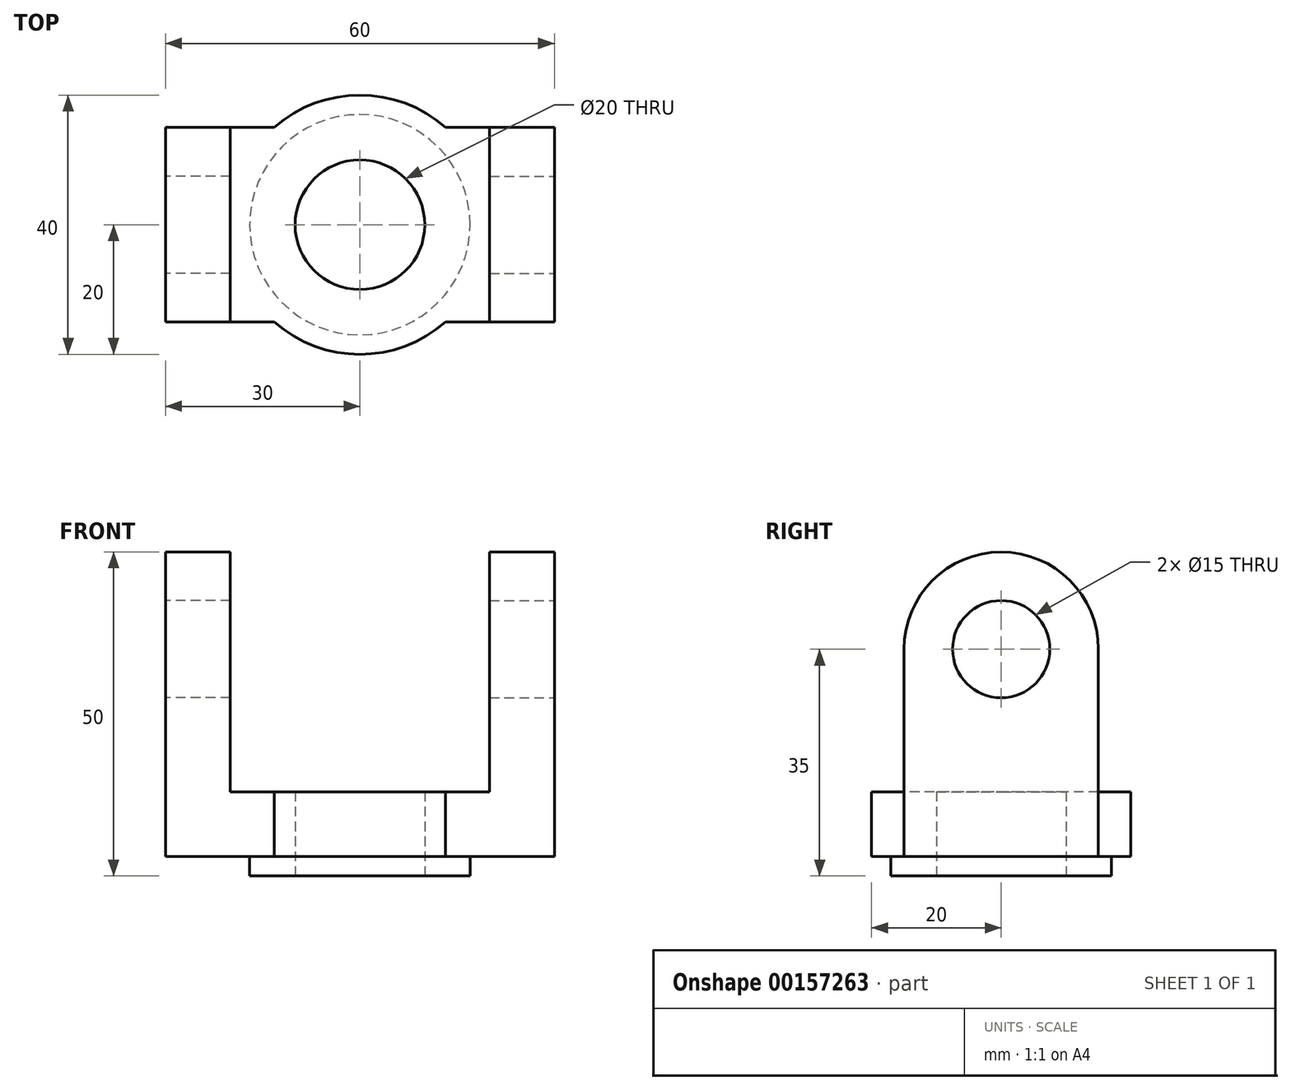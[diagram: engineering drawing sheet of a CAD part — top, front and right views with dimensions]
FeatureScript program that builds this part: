
annotation { "Feature Type Name" : "Feature", "Feature Type Description" : "" }
export const myFeature = defineFeature(function(context is Context, id is Id, definition is map)
    precondition{}
    {
        {
            var Q0;
            Q0=qCreatedBy(makeId("Top.planeOp"),FACE);
            var sketch = newSketch(context, id + "F0", { "sketchPlane" : qUnion([Q0])});
            skCircle(sketch, "E0", {"center": v(0, 0) * mm, "radius": 10 * mm});
            skArc(sketch, "E1", {"start": v(-13.23, -15) * mm, "mid": v(0, -20) * mm, "end": v(13.23, -15) * mm});
            skLineSegment(sketch, "E2.bottom", {"start": v(30, 15) * mm, "end": v(13.23, 15) * mm});
            skLineSegment(sketch, "E2.top", {"start": v(30, -15) * mm, "end": v(13.23, -15) * mm});
            skLineSegment(sketch, "E2.left", {"start": v(30, 15) * mm, "end": v(30, -15) * mm});
            skLineSegment(sketch, "E2.right", {"start": v(-30, 15) * mm, "end": v(-30, -15) * mm});
            skArc(sketch, "E3.trimOffspring", {"start": v(13.23, 15) * mm, "mid": v(0, 20) * mm, "end": v(-13.23, 15) * mm});
            skLineSegment(sketch, "E4.trimOffspring", {"start": v(-13.23, -15) * mm, "end": v(-30, -15) * mm});
            skLineSegment(sketch, "E5.trimOffspring", {"start": v(-13.23, 15) * mm, "end": v(-30, 15) * mm});
            skSolve(sketch);
        }
        {
            var Q0;
            Q0 = qSketchRegion(id + "F0", true);
            extrude(context, id + "F1", {"entities" : qUnion([Q0]), "depth" : 10 * mm});
        }
        {
            var Q0;
            Q0=makeQuery(id+"F1.opExtrude","CAP_FACE",FACE,{"disambiguationData":[OSD([sQuery(id+"F0.wireOp",EDGE,"E0"),sQuery(id+"F0.wireOp",EDGE,"E1"),sQuery(id+"F0.wireOp",EDGE,"E2.bottom"),sQuery(id+"F0.wireOp",EDGE,"E2.top"),sQuery(id+"F0.wireOp",EDGE,"E2.left"),sQuery(id+"F0.wireOp",EDGE,"E2.right"),sQuery(id+"F0.wireOp",EDGE,"E3.trimOffspring"),sQuery(id+"F0.wireOp",EDGE,"E4.trimOffspring"),sQuery(id+"F0.wireOp",EDGE,"E5.trimOffspring")])],"isStart":true});
            var sketch = newSketch(context, id + "F2", { "sketchPlane" : qUnion([Q0])});
            skCircle(sketch, "E6", {"center": v(0, 0) * mm, "radius": 17 * mm});
            skCircle(sketch, "E7", {"center": v(0, 0) * mm, "radius": 10 * mm});
            skSolve(sketch);
        }
        {
            var Q0;
            Q0 = qSketchRegion(id + "F2", true);
            extrude(context, id + "F3", {"entities" : qUnion([Q0]), "operationType" : NewBodyOperationType.ADD, "depth" : 3 * mm});
        }
        {
            var Q0;
            Q0=makeQuery(id+"F1.opExtrude","SWEPT_FACE",FACE,{"disambiguationData":[OSD([sQuery(id+"F0.wireOp",EDGE,"E2.right")])]});
            var sketch = newSketch(context, id + "F4", { "sketchPlane" : qUnion([Q0])});
            skLineSegment(sketch, "E8", {"start": v(-15, 10) * mm, "end": v(-15, 32) * mm});
            skLineSegment(sketch, "E9", {"start": v(15, 10) * mm, "end": v(15, 32) * mm});
            skArc(sketch, "E10", {"start": v(15, 32) * mm, "mid": v(0, 47) * mm, "end": v(-15, 32) * mm});
            skCircle(sketch, "E11", {"center": v(0, 32) * mm, "radius": 7.5 * mm});
            skSolve(sketch);
        }
        {
            var Q0;
            Q0=makeQuery(id+"F4.imprint","IMPRINT",FACE,{"disambiguationData":[TD([[makeQuery(id+"F4.imprint","IMPRINT",EDGE,{"derivedFrom":sQuery(id+"F4.wireOp",EDGE,"E8")}),-1.0]])]});
            extrude(context, id + "F5", {"entities" : qUnion([Q0]), "operationType" : NewBodyOperationType.ADD, "oppositeDirection" : true, "depth" : 10 * mm});
        }
        {
            var Q0;
            Q0=makeQuery(id+"F1.opExtrude","SWEPT_FACE",FACE,{"disambiguationData":[OSD([sQuery(id+"F0.wireOp",EDGE,"E2.left")])]});
            var sketch = newSketch(context, id + "F6", { "sketchPlane" : qUnion([Q0])});
            skLineSegment(sketch, "E12", {"start": v(-15, 10) * mm, "end": v(-15, 32) * mm});
            skLineSegment(sketch, "E13", {"start": v(15, 10) * mm, "end": v(15, 32) * mm});
            skArc(sketch, "E14", {"start": v(15, 32) * mm, "mid": v(0, 47) * mm, "end": v(-15, 32) * mm});
            skCircle(sketch, "E15", {"center": v(0, 32) * mm, "radius": 7.5 * mm});
            skSolve(sketch);
        }
        {
            var Q0;
            Q0=makeQuery(id+"F6.imprint","IMPRINT",FACE,{"disambiguationData":[TD([[makeQuery(id+"F6.imprint","IMPRINT",EDGE,{"derivedFrom":sQuery(id+"F6.wireOp",EDGE,"E12")}),-1.0]])]});
            extrude(context, id + "F7", {"entities" : qUnion([Q0]), "operationType" : NewBodyOperationType.ADD, "oppositeDirection" : true, "depth" : 10 * mm});
        }
    });
